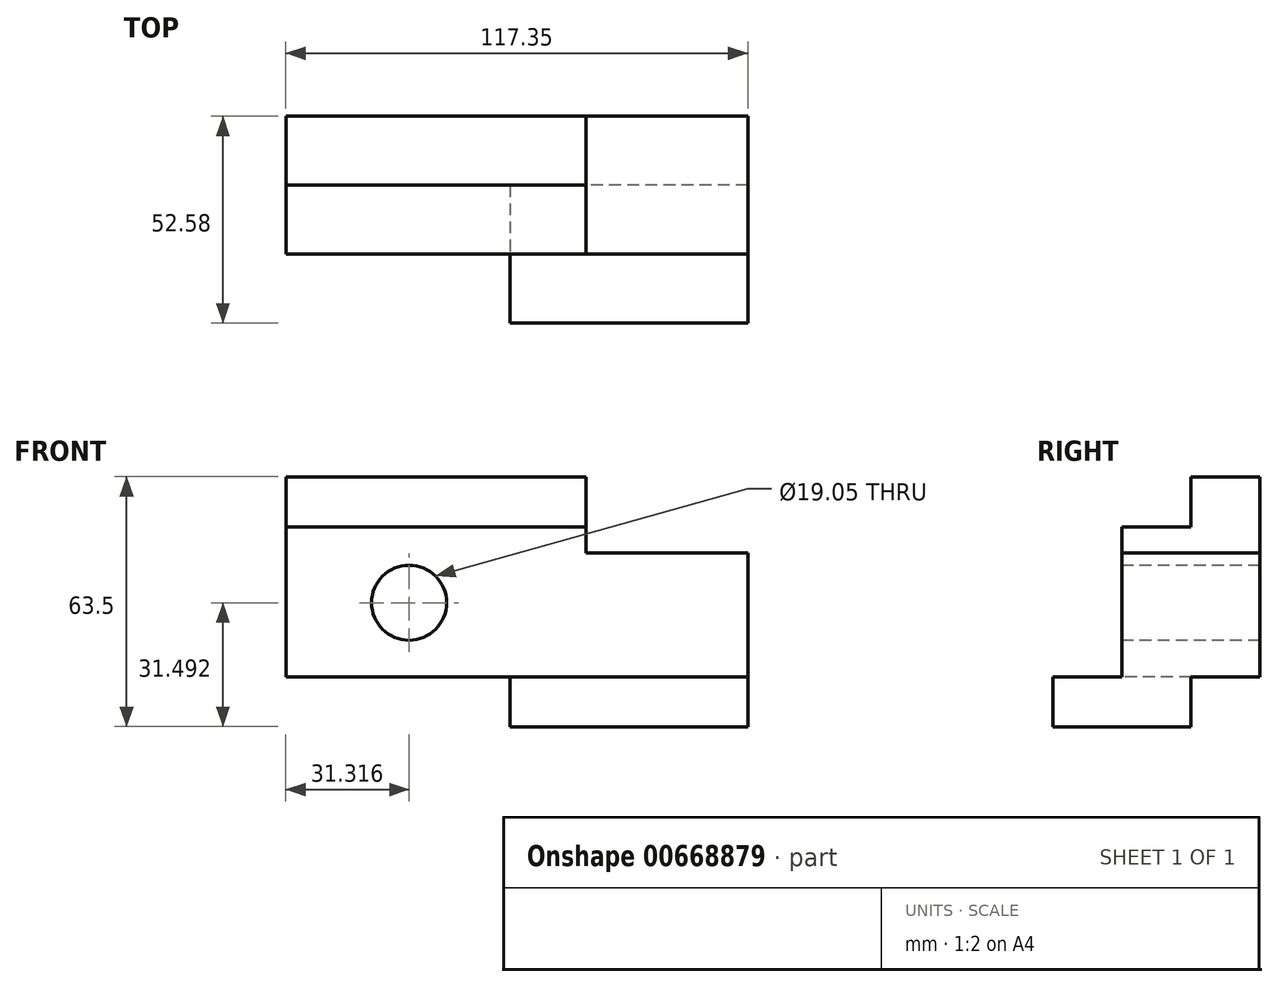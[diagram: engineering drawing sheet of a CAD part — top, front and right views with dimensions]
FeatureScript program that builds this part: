
annotation { "Feature Type Name" : "Feature", "Feature Type Description" : "" }
export const myFeature = defineFeature(function(context is Context, id is Id, definition is map)
    precondition{}
    {
        {
            var Q0;
            Q0=qCreatedBy(makeId("Front.planeOp"),FACE);
            var sketch = newSketch(context, id + "F0", { "sketchPlane" : qUnion([Q0])});
            skLineSegment(sketch, "E0.bottom", {"start": v(-39.23, 24.05) * mm, "end": v(78.12, 24.05) * mm});
            skLineSegment(sketch, "E0.top", {"start": v(-39.23, -26.75) * mm, "end": v(78.12, -26.75) * mm});
            skLineSegment(sketch, "E0.left", {"start": v(-39.23, 24.05) * mm, "end": v(-39.23, -26.75) * mm});
            skLineSegment(sketch, "E0.right", {"start": v(78.12, 24.05) * mm, "end": v(78.12, -26.75) * mm});
            skSolve(sketch);
        }
        {
            var Q0;
            Q0 = qSketchRegion(id + "F0", true);
            extrude(context, id + "F1", {"entities" : qUnion([Q0]), "depth" : 25.4 * mm, "offsetDistance" : 25.4 * mm});
        }
        {
            var Q0;
            Q0=makeQuery(id+"F1.opExtrude","CAP_FACE",FACE,{"disambiguationData":[OSD([sQuery(id+"F0.wireOp",EDGE,"E0.bottom"),sQuery(id+"F0.wireOp",EDGE,"E0.top"),sQuery(id+"F0.wireOp",EDGE,"E0.left"),sQuery(id+"F0.wireOp",EDGE,"E0.right")])],"isStart":false});
            var sketch = newSketch(context, id + "F2", { "sketchPlane" : qUnion([Q0])});
            skCircle(sketch, "E1", {"center": v(-7.91, -7.96) * mm, "radius": 9.53 * mm});
            skSolve(sketch);
        }
        {
            var Q0;
            Q0 = qSketchRegion(id + "F0", true);
            extrude(context, id + "F3", {"entities" : qUnion([Q0]), "operationType" : NewBodyOperationType.ADD, "oppositeDirection" : true, "depth" : 9.65 * mm, "offsetDistance" : 25.4 * mm});
        }
        {
            var Q0;
            Q0 = qSketchRegion(id + "F2", true);
            extrude(context, id + "F4", {"entities" : qUnion([Q0]), "operationType" : NewBodyOperationType.REMOVE, "endBound" : BoundingType.THROUGH_ALL, "oppositeDirection" : true, "depth" : 25.4 * mm, "offsetDistance" : 25.4 * mm});
        }
        {
            var Q0;
            {var subQ0=sQuery(id+"F0.wireOp",EDGE,"E0.top");Q0=makeQuery(id+"F3.boolean.opBoolean","MERGE",FACE,{"derivedFrom":[makeQuery(id+"F1.opExtrude","SWEPT_FACE",FACE,{"disambiguationData":[OSD([subQ0])]}),makeQuery(id+"F3.opExtrude","SWEPT_FACE",FACE,{"disambiguationData":[OSD([subQ0])]})]});}
            var sketch = newSketch(context, id + "F5", { "sketchPlane" : qUnion([Q0])});
            skLineSegment(sketch, "E2.bottom", {"start": v(78.12, 7.87) * mm, "end": v(17.67, 7.87) * mm});
            skLineSegment(sketch, "E2.top", {"start": v(78.12, 42.93) * mm, "end": v(17.67, 42.93) * mm});
            skLineSegment(sketch, "E2.left", {"start": v(78.12, 7.87) * mm, "end": v(78.12, 42.93) * mm});
            skLineSegment(sketch, "E2.right", {"start": v(17.67, 7.87) * mm, "end": v(17.67, 42.93) * mm});
            skSolve(sketch);
        }
        {
            var Q0;
            Q0 = qSketchRegion(id + "F5", true);
            extrude(context, id + "F6", {"entities" : qUnion([Q0]), "operationType" : NewBodyOperationType.ADD, "depth" : 12.7 * mm, "offsetDistance" : 25.4 * mm});
        }
        {
            var Q0;
            {var subQ0=sQuery(id+"F0.wireOp",EDGE,"E0.bottom");Q0=makeQuery(id+"F3.boolean.opBoolean","MERGE",FACE,{"derivedFrom":[makeQuery(id+"F1.opExtrude","SWEPT_FACE",FACE,{"disambiguationData":[OSD([subQ0])]}),makeQuery(id+"F3.opExtrude","SWEPT_FACE",FACE,{"disambiguationData":[OSD([subQ0])]})]});}
            var sketch = newSketch(context, id + "F7", { "sketchPlane" : qUnion([Q0])});
            skLineSegment(sketch, "E3.bottom", {"start": v(-39.23, -25.4) * mm, "end": v(36.97, -25.4) * mm});
            skLineSegment(sketch, "E3.top", {"start": v(-39.23, -7.87) * mm, "end": v(36.97, -7.87) * mm});
            skLineSegment(sketch, "E3.left", {"start": v(-39.23, -25.4) * mm, "end": v(-39.23, -7.87) * mm});
            skLineSegment(sketch, "E3.right", {"start": v(36.97, -25.4) * mm, "end": v(36.97, -7.87) * mm});
            skSolve(sketch);
        }
        {
            var Q0;
            Q0 = qSketchRegion(id + "F7", true);
            extrude(context, id + "F8", {"entities" : qUnion([Q0]), "operationType" : NewBodyOperationType.REMOVE, "oppositeDirection" : true, "depth" : 12.7 * mm, "offsetDistance" : 25.4 * mm});
        }
        {
            var Q0;
            {var subQ0=sQuery(id+"F0.wireOp",EDGE,"E0.bottom");Q0=makeQuery(id+"F3.boolean.opBoolean","MERGE",FACE,{"derivedFrom":[makeQuery(id+"F1.opExtrude","SWEPT_FACE",FACE,{"disambiguationData":[OSD([subQ0])]}),makeQuery(id+"F3.opExtrude","SWEPT_FACE",FACE,{"disambiguationData":[OSD([subQ0])]})]});}
            var sketch = newSketch(context, id + "F9", { "sketchPlane" : qUnion([Q0])});
            skLineSegment(sketch, "E4.bottom", {"start": v(36.97, -25.4) * mm, "end": v(78.12, -25.4) * mm});
            skLineSegment(sketch, "E4.top", {"start": v(36.97, 9.65) * mm, "end": v(78.12, 9.65) * mm});
            skLineSegment(sketch, "E4.left", {"start": v(36.97, -25.4) * mm, "end": v(36.97, 9.65) * mm});
            skLineSegment(sketch, "E4.right", {"start": v(78.12, -25.4) * mm, "end": v(78.12, 9.65) * mm});
            skSolve(sketch);
        }
        {
            var Q0;
            Q0 = qSketchRegion(id + "F9", true);
            extrude(context, id + "F10", {"entities" : qUnion([Q0]), "operationType" : NewBodyOperationType.REMOVE, "oppositeDirection" : true, "depth" : 19.3 * mm, "offsetDistance" : 25.4 * mm});
        }
    });
